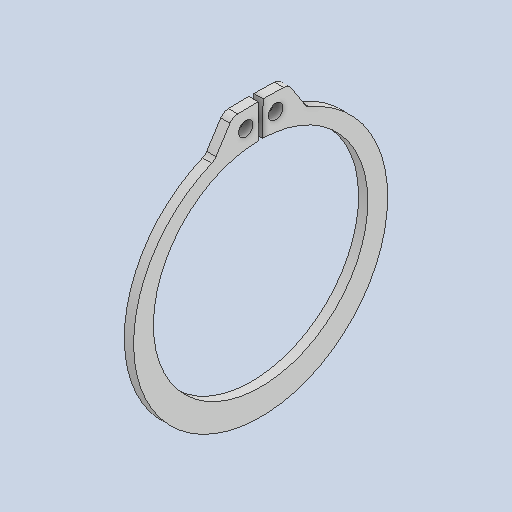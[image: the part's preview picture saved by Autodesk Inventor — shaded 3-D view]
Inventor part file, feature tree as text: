
AUTODESK INVENTOR PART (.ipt)
format: ipt  version: 2023 (Build 270158000, 158)  size: 114,176 bytes
history: native  units: in
note: dims shown in document units (in); Inventor stores cm internally (conversion verified against a paired STEP export)
features: fillet x1
ambient origin geometry x8: Origin, YZ Plane, XZ Plane, XY Plane, X Axis, Y Axis, Z Axis, Center Point
bodies: Solid1 (feature_tree)
feature tree (1):
  fillet  "Fillet1"  [1 undecoded]
note: 1 required parameter value undecoded (feature->parameter linkage not recoverable at this tier; creation-order binding heuristic only, values carry confidence <= 0.55)
